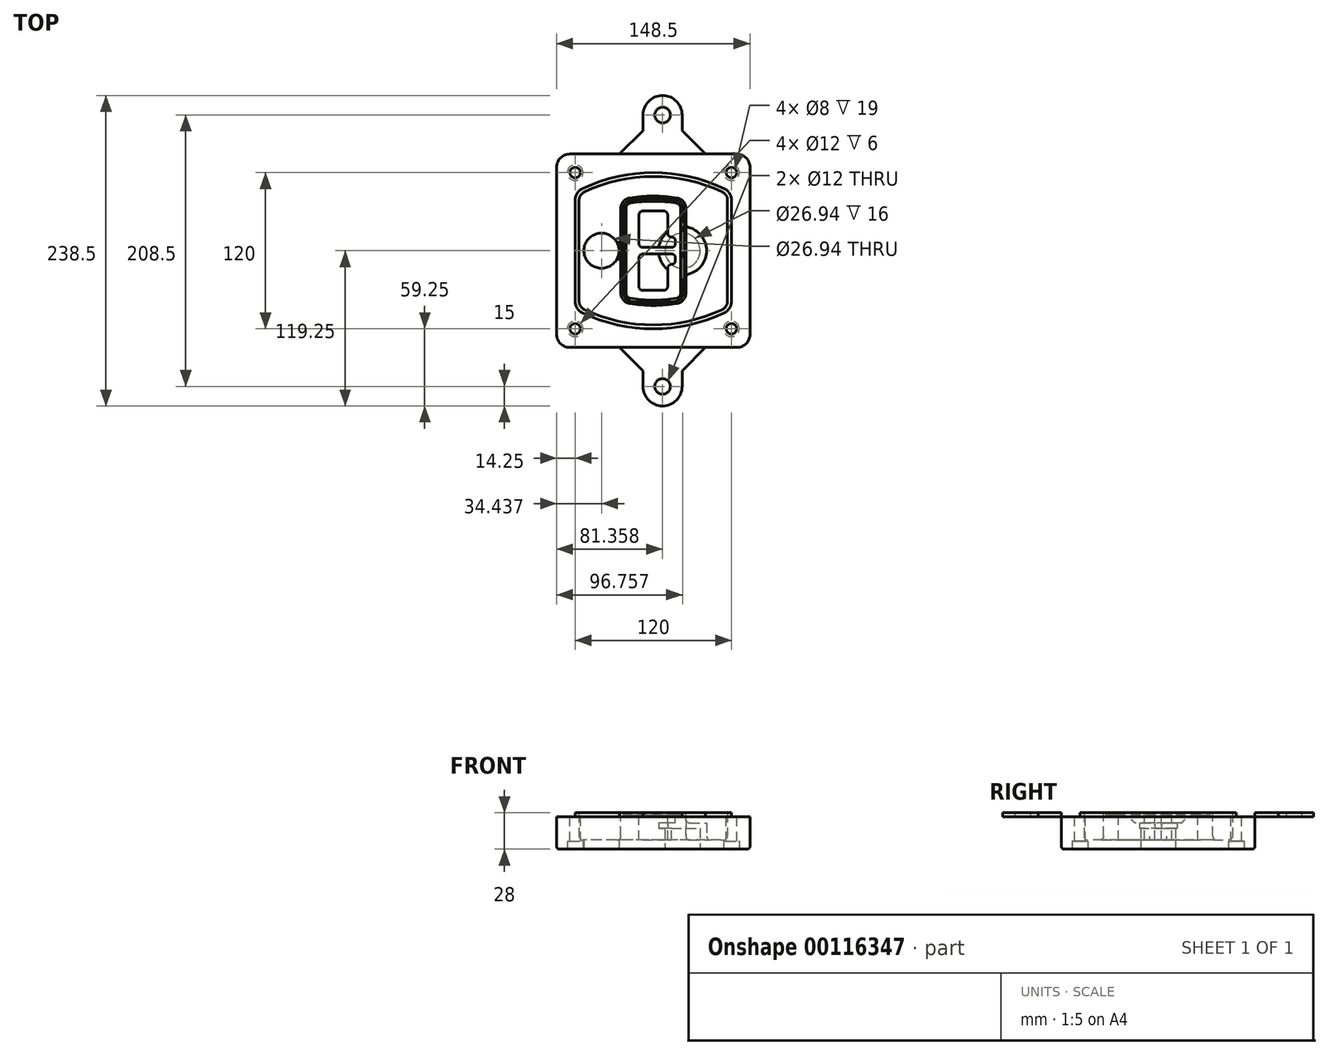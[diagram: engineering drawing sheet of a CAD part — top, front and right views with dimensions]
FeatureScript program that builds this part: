
annotation { "Feature Type Name" : "Feature", "Feature Type Description" : "" }
export const myFeature = defineFeature(function(context is Context, id is Id, definition is map)
    precondition{}
    {
        {
            var Q0;
            Q0=qCreatedBy(makeId("Top.planeOp"),FACE);
            var sketch = newSketch(context, id + "F0", { "sketchPlane" : qUnion([Q0])});
            skPoint(sketch, "E0.rect.middle", {"position": v(0, 0) * mm});
            skLineSegment(sketch, "E1.bottom", {"start": v(-64.25, -74.25) * mm, "end": v(64.25, -74.25) * mm});
            skLineSegment(sketch, "E1.top", {"start": v(-64.25, 74.25) * mm, "end": v(64.25, 74.25) * mm});
            skLineSegment(sketch, "E1.left", {"start": v(-74.25, -64.25) * mm, "end": v(-74.25, 64.25) * mm});
            skLineSegment(sketch, "E1.right", {"start": v(74.25, -64.25) * mm, "end": v(74.25, 64.25) * mm});
            skLineSegment(sketch, "E2", {"start": v(-74.25, 74.25) * mm, "end": v(74.25, -74.25) * mm, "construction": true});
            skLineSegment(sketch, "E3", {"start": v(74.25, 74.25) * mm, "end": v(-74.25, -74.25) * mm, "construction": true});
            skCircle(sketch, "E4", {"center": v(-60, 60) * mm, "radius": 4 * mm});
            skCircle(sketch, "E5", {"center": v(60, 60) * mm, "radius": 4 * mm});
            skCircle(sketch, "E6", {"center": v(60, -60) * mm, "radius": 4 * mm});
            skCircle(sketch, "E7", {"center": v(-60, -60) * mm, "radius": 4 * mm});
            skLineSegment(sketch, "E8", {"start": v(-60, 60) * mm, "end": v(60, 60) * mm, "construction": true});
            skLineSegment(sketch, "E9", {"start": v(60, 60) * mm, "end": v(60, -60) * mm, "construction": true});
            skLineSegment(sketch, "E10", {"start": v(60, -60) * mm, "end": v(-60, -60) * mm, "construction": true});
            skLineSegment(sketch, "E11", {"start": v(-60, -60) * mm, "end": v(-60, 60) * mm, "construction": true});
            skLineSegment(sketch, "E12", {"start": v(-60, 38.83) * mm, "end": v(-60, -38.83) * mm});
            skLineSegment(sketch, "E13", {"start": v(60, 38.83) * mm, "end": v(60, -38.83) * mm});
            skArc(sketch, "E14", {"start": v(54.26, 47.88) * mm, "mid": v(0, 60) * mm, "end": v(-54.26, 47.88) * mm});
            skArc(sketch, "E15", {"start": v(-54.26, -47.88) * mm, "mid": v(0, -60) * mm, "end": v(54.26, -47.88) * mm});
            skLineSegment(sketch, "E16", {"start": v(-60, 0) * mm, "end": v(60, 0) * mm, "construction": true});
            skPoint(sketch, "E17.visualSharp", {"position": v(-60, -45) * mm});
            skArc(sketch, "E17.filletArc", {"start": v(-60, -38.83) * mm, "mid": v(-58.44, -44.2) * mm, "end": v(-54.26, -47.88) * mm});
            skPoint(sketch, "E18.visualSharp", {"position": v(-60, 45) * mm});
            skArc(sketch, "E18.filletArc", {"start": v(-54.26, 47.88) * mm, "mid": v(-58.44, 44.2) * mm, "end": v(-60, 38.83) * mm});
            skPoint(sketch, "E19.visualSharp", {"position": v(60, 45) * mm});
            skArc(sketch, "E19.filletArc", {"start": v(60, 38.83) * mm, "mid": v(58.44, 44.2) * mm, "end": v(54.26, 47.88) * mm});
            skPoint(sketch, "E20.visualSharp", {"position": v(60, -45) * mm});
            skArc(sketch, "E20.filletArc", {"start": v(54.26, -47.88) * mm, "mid": v(58.44, -44.2) * mm, "end": v(60, -38.83) * mm});
            skPoint(sketch, "E21.visualSharp", {"position": v(-74.25, 74.25) * mm});
            skArc(sketch, "E21.filletArc", {"start": v(-64.25, 74.25) * mm, "mid": v(-71.32, 71.32) * mm, "end": v(-74.25, 64.25) * mm});
            skPoint(sketch, "E22.visualSharp", {"position": v(74.25, 74.25) * mm});
            skArc(sketch, "E22.filletArc", {"start": v(74.25, 64.25) * mm, "mid": v(71.32, 71.32) * mm, "end": v(64.25, 74.25) * mm});
            skPoint(sketch, "E23.visualSharp", {"position": v(74.25, -74.25) * mm});
            skArc(sketch, "E23.filletArc", {"start": v(64.25, -74.25) * mm, "mid": v(71.32, -71.32) * mm, "end": v(74.25, -64.25) * mm});
            skPoint(sketch, "E24.visualSharp", {"position": v(-74.25, -74.25) * mm});
            skArc(sketch, "E24.filletArc", {"start": v(-74.25, -64.25) * mm, "mid": v(-71.32, -71.32) * mm, "end": v(-64.25, -74.25) * mm});
            skArc(sketch, "E25.0", {"start": v(57, 38.83) * mm, "mid": v(55.9, 42.58) * mm, "end": v(52.98, 45.17) * mm});
            skLineSegment(sketch, "E25.1", {"start": v(57, 38.83) * mm, "end": v(57, -38.83) * mm});
            skArc(sketch, "E25.2", {"start": v(52.98, -45.17) * mm, "mid": v(55.9, -42.58) * mm, "end": v(57, -38.83) * mm});
            skArc(sketch, "E25.3", {"start": v(-52.98, -45.17) * mm, "mid": v(0, -57) * mm, "end": v(52.98, -45.17) * mm});
            skArc(sketch, "E25.4", {"start": v(-57, -38.83) * mm, "mid": v(-55.9, -42.58) * mm, "end": v(-52.98, -45.17) * mm});
            skArc(sketch, "E25.5", {"start": v(52.98, 45.17) * mm, "mid": v(0, 57) * mm, "end": v(-52.98, 45.17) * mm});
            skLineSegment(sketch, "E25.6", {"start": v(-57, 38.83) * mm, "end": v(-57, -38.83) * mm});
            skArc(sketch, "E25.7", {"start": v(-52.98, 45.17) * mm, "mid": v(-55.9, 42.58) * mm, "end": v(-57, 38.83) * mm});
            skArc(sketch, "E26.0", {"start": v(-55.96, 51.5) * mm, "mid": v(-61.82, 46.33) * mm, "end": v(-64, 38.83) * mm});
            skArc(sketch, "E26.1", {"start": v(55.96, 51.5) * mm, "mid": v(0, 64) * mm, "end": v(-55.96, 51.5) * mm});
            skArc(sketch, "E26.2", {"start": v(64, 38.83) * mm, "mid": v(61.82, 46.33) * mm, "end": v(55.96, 51.5) * mm});
            skLineSegment(sketch, "E26.3", {"start": v(64, 38.83) * mm, "end": v(64, -38.83) * mm});
            skArc(sketch, "E26.4", {"start": v(55.96, -51.5) * mm, "mid": v(61.82, -46.33) * mm, "end": v(64, -38.83) * mm});
            skLineSegment(sketch, "E26.5", {"start": v(-64, 38.83) * mm, "end": v(-64, -38.83) * mm});
            skArc(sketch, "E26.6", {"start": v(-55.96, -51.5) * mm, "mid": v(0, -64) * mm, "end": v(55.96, -51.5) * mm});
            skArc(sketch, "E26.7", {"start": v(-64, -38.83) * mm, "mid": v(-61.82, -46.33) * mm, "end": v(-55.96, -51.5) * mm});
            skSolve(sketch);
        }
        {
            var Q0;
            Q0=makeQuery(id+"F0.imprint","IMPRINT",FACE,{"disambiguationData":[TD([[makeQuery(id+"F0.imprint","IMPRINT",EDGE,{"derivedFrom":sQuery(id+"F0.wireOp",EDGE,"E1.bottom")}),1.0]])]});
            var Q1;
            Q1=makeQuery(id+"F0.imprint","IMPRINT",FACE,{"disambiguationData":[TD([[makeQuery(id+"F0.imprint","IMPRINT",EDGE,{"derivedFrom":sQuery(id+"F0.wireOp",EDGE,"E12")}),1.0]])]});
            var Q2;
            Q2=makeQuery(id+"F0.imprint","IMPRINT",FACE,{"disambiguationData":[TD([[makeQuery(id+"F0.imprint","IMPRINT",EDGE,{"derivedFrom":sQuery(id+"F0.wireOp",EDGE,"E25.0")}),1.0]])]});
            var Q3;
            Q3=makeQuery(id+"F0.imprint","IMPRINT",FACE,{"disambiguationData":[TD([[makeQuery(id+"F0.imprint","IMPRINT",EDGE,{"derivedFrom":sQuery(id+"F0.wireOp",EDGE,"E12")}),-1.0]])]});
            extrude(context, id + "F1", {"entities" : qUnion([Q0, Q1, Q2, Q3]), "oppositeDirection" : true, "depth" : 25 * mm});
        }
        {
            var Q0;
            Q0=makeQuery(id+"F0.imprint","IMPRINT",FACE,{"disambiguationData":[TD([[makeQuery(id+"F0.imprint","IMPRINT",EDGE,{"derivedFrom":sQuery(id+"F0.wireOp",EDGE,"E12")}),1.0]])]});
            extrude(context, id + "F2", {"entities" : qUnion([Q0]), "operationType" : NewBodyOperationType.ADD, "depth" : 3 * mm});
        }
        {
            var Q0;
            Q0=makeQuery(id+"F0.imprint","IMPRINT",FACE,{"disambiguationData":[TD([[makeQuery(id+"F0.imprint","IMPRINT",EDGE,{"derivedFrom":sQuery(id+"F0.wireOp",EDGE,"E25.0")}),1.0]])]});
            extrude(context, id + "F3", {"entities" : qUnion([Q0]), "operationType" : NewBodyOperationType.REMOVE, "oppositeDirection" : true, "depth" : 18 * mm});
        }
        {
            var Q0;
            Q0=makeQuery(id+"F2.opExtrude","CAP_FACE",FACE,{"disambiguationData":[OSD([sQuery(id+"F0.wireOp",EDGE,"E12"),sQuery(id+"F0.wireOp",EDGE,"E13"),sQuery(id+"F0.wireOp",EDGE,"E14"),sQuery(id+"F0.wireOp",EDGE,"E15"),sQuery(id+"F0.wireOp",EDGE,"E17.filletArc"),sQuery(id+"F0.wireOp",EDGE,"E18.filletArc"),sQuery(id+"F0.wireOp",EDGE,"E19.filletArc"),sQuery(id+"F0.wireOp",EDGE,"E20.filletArc"),sQuery(id+"F0.wireOp",EDGE,"E25.0"),sQuery(id+"F0.wireOp",EDGE,"E25.1"),sQuery(id+"F0.wireOp",EDGE,"E25.2"),sQuery(id+"F0.wireOp",EDGE,"E25.3"),sQuery(id+"F0.wireOp",EDGE,"E25.4"),sQuery(id+"F0.wireOp",EDGE,"E25.5"),sQuery(id+"F0.wireOp",EDGE,"E25.6"),sQuery(id+"F0.wireOp",EDGE,"E25.7")])],"isStart":false});
            var sketch = newSketch(context, id + "F4", { "sketchPlane" : qUnion([Q0])});
            skArc(sketch, "E27.0", {"start": v(-18.34, -40.45) * mm, "mid": v(0, -42) * mm, "end": v(18.34, -40.45) * mm});
            skArc(sketch, "E28.0", {"start": v(18.34, 40.45) * mm, "mid": v(0, 42) * mm, "end": v(-18.34, 40.45) * mm});
            skLineSegment(sketch, "E29", {"start": v(-25, 32.57) * mm, "end": v(-25, -32.57) * mm});
            skLineSegment(sketch, "E30", {"start": v(25, 32.57) * mm, "end": v(25, -32.57) * mm});
            skLineSegment(sketch, "E31", {"start": v(-25, 39.1) * mm, "end": v(25, 39.1) * mm, "construction": true});
            skLineSegment(sketch, "E32", {"start": v(-25, -39.1) * mm, "end": v(25, -39.1) * mm, "construction": true});
            skPoint(sketch, "E33.visualSharp", {"position": v(-25, 39.1) * mm});
            skArc(sketch, "E33.filletArc", {"start": v(-18.34, 40.45) * mm, "mid": v(-23.11, 37.73) * mm, "end": v(-25, 32.57) * mm});
            skPoint(sketch, "E34.visualSharp", {"position": v(25, 39.1) * mm});
            skArc(sketch, "E34.filletArc", {"start": v(25, 32.57) * mm, "mid": v(23.11, 37.73) * mm, "end": v(18.34, 40.45) * mm});
            skPoint(sketch, "E35.visualSharp", {"position": v(25, -39.1) * mm});
            skArc(sketch, "E35.filletArc", {"start": v(18.34, -40.45) * mm, "mid": v(23.11, -37.73) * mm, "end": v(25, -32.57) * mm});
            skPoint(sketch, "E36.visualSharp", {"position": v(-25, -39.1) * mm});
            skArc(sketch, "E36.filletArc", {"start": v(-25, -32.57) * mm, "mid": v(-23.11, -37.73) * mm, "end": v(-18.34, -40.45) * mm});
            skArc(sketch, "E37.0", {"start": v(52.98, 45.17) * mm, "mid": v(0, 57) * mm, "end": v(-52.98, 45.17) * mm});
            skArc(sketch, "E37.1", {"start": v(-52.98, 45.17) * mm, "mid": v(-55.9, 42.58) * mm, "end": v(-57, 38.83) * mm});
            skLineSegment(sketch, "E37.2", {"start": v(-57, 38.83) * mm, "end": v(-57, -38.83) * mm});
            skArc(sketch, "E37.3", {"start": v(-57, -38.83) * mm, "mid": v(-55.9, -42.58) * mm, "end": v(-52.98, -45.17) * mm});
            skArc(sketch, "E37.4", {"start": v(-52.98, -45.17) * mm, "mid": v(0, -57) * mm, "end": v(52.98, -45.17) * mm});
            skArc(sketch, "E37.5", {"start": v(52.98, -45.17) * mm, "mid": v(55.9, -42.58) * mm, "end": v(57, -38.83) * mm});
            skLineSegment(sketch, "E37.6", {"start": v(57, 38.83) * mm, "end": v(57, -38.83) * mm});
            skArc(sketch, "E37.7", {"start": v(57, 38.83) * mm, "mid": v(55.9, 42.58) * mm, "end": v(52.98, 45.17) * mm});
            skLineSegment(sketch, "E38.0", {"start": v(23, 32.57) * mm, "end": v(23, -32.57) * mm});
            skArc(sketch, "E38.1", {"start": v(18, -38.48) * mm, "mid": v(21.58, -36.44) * mm, "end": v(23, -32.57) * mm});
            skArc(sketch, "E38.2", {"start": v(-18, -38.48) * mm, "mid": v(0, -40) * mm, "end": v(18, -38.48) * mm});
            skArc(sketch, "E38.3", {"start": v(-23, -32.57) * mm, "mid": v(-21.58, -36.44) * mm, "end": v(-18, -38.48) * mm});
            skLineSegment(sketch, "E38.4", {"start": v(-23, 32.57) * mm, "end": v(-23, -32.57) * mm});
            skArc(sketch, "E38.5", {"start": v(23, 32.57) * mm, "mid": v(21.58, 36.44) * mm, "end": v(18, 38.48) * mm});
            skArc(sketch, "E38.6", {"start": v(-18, 38.48) * mm, "mid": v(-21.58, 36.44) * mm, "end": v(-23, 32.57) * mm});
            skArc(sketch, "E38.7", {"start": v(18, 38.48) * mm, "mid": v(0, 40) * mm, "end": v(-18, 38.48) * mm});
            skArc(sketch, "E39.0", {"start": v(21, 32.57) * mm, "mid": v(20.06, 35.15) * mm, "end": v(17.67, 36.5) * mm});
            skLineSegment(sketch, "E39.1", {"start": v(21, 32.57) * mm, "end": v(21, -32.57) * mm});
            skArc(sketch, "E39.2", {"start": v(17.67, -36.5) * mm, "mid": v(20.06, -35.15) * mm, "end": v(21, -32.57) * mm});
            skArc(sketch, "E39.3", {"start": v(-17.67, -36.5) * mm, "mid": v(0, -38) * mm, "end": v(17.67, -36.5) * mm});
            skArc(sketch, "E39.4", {"start": v(-21, -32.57) * mm, "mid": v(-20.06, -35.15) * mm, "end": v(-17.67, -36.5) * mm});
            skArc(sketch, "E39.5", {"start": v(17.67, 36.5) * mm, "mid": v(0, 38) * mm, "end": v(-17.67, 36.5) * mm});
            skLineSegment(sketch, "E39.6", {"start": v(-21, 32.57) * mm, "end": v(-21, -32.57) * mm});
            skArc(sketch, "E39.7", {"start": v(-17.67, 36.5) * mm, "mid": v(-20.06, 35.15) * mm, "end": v(-21, 32.57) * mm});
            skLineSegment(sketch, "E40", {"start": v(-25, 0) * mm, "end": v(25, 0) * mm, "construction": true});
            skLineSegment(sketch, "E41", {"start": v(-11, 5.5) * mm, "end": v(-11, 27.5) * mm});
            skLineSegment(sketch, "E42", {"start": v(-8, 30.5) * mm, "end": v(8, 30.5) * mm});
            skLineSegment(sketch, "E43", {"start": v(11, 27.5) * mm, "end": v(11, 13.5) * mm});
            skLineSegment(sketch, "E44", {"start": v(14, 10.5) * mm, "end": v(14, 10.5) * mm});
            skLineSegment(sketch, "E45", {"start": v(17, 7.5) * mm, "end": v(17, 5.5) * mm});
            skLineSegment(sketch, "E46", {"start": v(14, 2.5) * mm, "end": v(-8, 2.5) * mm});
            skPoint(sketch, "E47.visualSharp", {"position": v(-11, 30.5) * mm});
            skArc(sketch, "E47.filletArc", {"start": v(-8, 30.5) * mm, "mid": v(-10.12, 29.62) * mm, "end": v(-11, 27.5) * mm});
            skPoint(sketch, "E48.visualSharp", {"position": v(11, 30.5) * mm});
            skArc(sketch, "E48.filletArc", {"start": v(11, 27.5) * mm, "mid": v(10.12, 29.62) * mm, "end": v(8, 30.5) * mm});
            skPoint(sketch, "E49.visualSharp", {"position": v(11, 10.5) * mm});
            skArc(sketch, "E49.filletArc", {"start": v(11, 13.5) * mm, "mid": v(11.88, 11.38) * mm, "end": v(14, 10.5) * mm});
            skPoint(sketch, "E50.visualSharp", {"position": v(17, 10.5) * mm});
            skArc(sketch, "E50.filletArc", {"start": v(17, 7.5) * mm, "mid": v(16.12, 9.62) * mm, "end": v(14, 10.5) * mm});
            skPoint(sketch, "E51.visualSharp", {"position": v(17, 2.5) * mm});
            skArc(sketch, "E51.filletArc", {"start": v(14, 2.5) * mm, "mid": v(16.12, 3.38) * mm, "end": v(17, 5.5) * mm});
            skPoint(sketch, "E52.visualSharp", {"position": v(-11, 2.5) * mm});
            skArc(sketch, "E52.filletArc", {"start": v(-11, 5.5) * mm, "mid": v(-10.12, 3.38) * mm, "end": v(-8, 2.5) * mm});
            skLineSegment(sketch, "E53.0.MirrorCS", {"start": v(14, -2.5) * mm, "end": v(-8, -2.5) * mm});
            skArc(sketch, "E54.0.MirrorCS", {"start": v(-11, -5.5) * mm, "mid": v(-10.12, -3.38) * mm, "end": v(-8, -2.5) * mm});
            skLineSegment(sketch, "E55.0.MirrorCS", {"start": v(-11, -5.5) * mm, "end": v(-11, -27.5) * mm});
            skArc(sketch, "E56.0.MirrorCS", {"start": v(-8, -30.5) * mm, "mid": v(-10.12, -29.62) * mm, "end": v(-11, -27.5) * mm});
            skLineSegment(sketch, "E57.0.MirrorCS", {"start": v(-8, -30.5) * mm, "end": v(8, -30.5) * mm});
            skArc(sketch, "E58.0.MirrorCS", {"start": v(11, -27.5) * mm, "mid": v(10.12, -29.62) * mm, "end": v(8, -30.5) * mm});
            skLineSegment(sketch, "E59.0.MirrorCS", {"start": v(11, -27.5) * mm, "end": v(11, -13.5) * mm});
            skArc(sketch, "E60.0.MirrorCS", {"start": v(11, -13.5) * mm, "mid": v(11.88, -11.38) * mm, "end": v(14, -10.5) * mm});
            skArc(sketch, "E61.0.MirrorCS", {"start": v(17, -7.5) * mm, "mid": v(16.12, -9.62) * mm, "end": v(14, -10.5) * mm});
            skLineSegment(sketch, "E62.0.MirrorCS", {"start": v(17, -7.5) * mm, "end": v(17, -5.5) * mm});
            skArc(sketch, "E63.0.MirrorCS", {"start": v(14, -2.5) * mm, "mid": v(16.12, -3.38) * mm, "end": v(17, -5.5) * mm});
            skSolve(sketch);
        }
        {
            var Q0;
            Q0=makeQuery(id+"F4.imprint","IMPRINT",FACE,{"disambiguationData":[TD([[makeQuery(id+"F4.imprint","IMPRINT",EDGE,{"derivedFrom":sQuery(id+"F4.wireOp",EDGE,"E27.0")}),1.0]])]});
            var Q1;
            Q1=makeQuery(id+"F4.imprint","IMPRINT",FACE,{"disambiguationData":[TD([[makeQuery(id+"F4.imprint","IMPRINT",EDGE,{"derivedFrom":sQuery(id+"F4.wireOp",EDGE,"E38.0")}),-1.0]])]});
            var Q2;
            Q2=makeQuery(id+"F4.imprint","IMPRINT",FACE,{"disambiguationData":[TD([[makeQuery(id+"F4.imprint","IMPRINT",EDGE,{"derivedFrom":sQuery(id+"F4.wireOp",EDGE,"E39.0")}),1.0]])]});
            extrude(context, id + "F5", {"entities" : qUnion([Q0, Q1, Q2]), "operationType" : NewBodyOperationType.ADD, "endBound" : BoundingType.UP_TO_NEXT, "oppositeDirection" : true, "depth" : 25 * mm});
        }
        {
            var Q0;
            Q0=makeQuery(id+"F4.imprint","IMPRINT",FACE,{"disambiguationData":[TD([[makeQuery(id+"F4.imprint","IMPRINT",EDGE,{"derivedFrom":sQuery(id+"F4.wireOp",EDGE,"E38.0")}),-1.0]])]});
            extrude(context, id + "F6", {"entities" : qUnion([Q0]), "operationType" : NewBodyOperationType.REMOVE, "oppositeDirection" : true, "depth" : 2 * mm});
        }
        {
            var Q0;
            Q0=makeQuery(id+"F1.opExtrude","CAP_FACE",FACE,{"disambiguationData":[OSD([sQuery(id+"F0.wireOp",EDGE,"E1.bottom"),sQuery(id+"F0.wireOp",EDGE,"E1.top"),sQuery(id+"F0.wireOp",EDGE,"E1.left"),sQuery(id+"F0.wireOp",EDGE,"E1.right"),sQuery(id+"F0.wireOp",EDGE,"E4"),sQuery(id+"F0.wireOp",EDGE,"E5"),sQuery(id+"F0.wireOp",EDGE,"E6"),sQuery(id+"F0.wireOp",EDGE,"E7"),sQuery(id+"F0.wireOp",EDGE,"E21.filletArc"),sQuery(id+"F0.wireOp",EDGE,"E22.filletArc"),sQuery(id+"F0.wireOp",EDGE,"E23.filletArc"),sQuery(id+"F0.wireOp",EDGE,"E24.filletArc")])],"isStart":false});
            var sketch = newSketch(context, id + "F7", { "sketchPlane" : qUnion([Q0])});
            skCircle(sketch, "E64", {"center": v(22.5, 0) * mm, "radius": 13.47 * mm});
            skCircle(sketch, "E65", {"center": v(-39.81, 0) * mm, "radius": 13.47 * mm});
            skLineSegment(sketch, "E66", {"start": v(74.25, 0) * mm, "end": v(-74.25, 0) * mm});
            skCircle(sketch, "E67", {"center": v(22.5, 0) * mm, "radius": 18.47 * mm});
            skCircle(sketch, "E68", {"center": v(60, -60) * mm, "radius": 6 * mm});
            skCircle(sketch, "E69", {"center": v(-60, -60) * mm, "radius": 6 * mm});
            skCircle(sketch, "E70", {"center": v(-60, 60) * mm, "radius": 6 * mm});
            skCircle(sketch, "E71", {"center": v(60, 60) * mm, "radius": 6 * mm});
            skSolve(sketch);
        }
        {
            var Q0;
            {var subQ1=sQuery(id+"F7.wireOp",EDGE,"E66");var subQ4=sQuery(id+"F7.wireOp",EDGE,"E64");var subQ6=makeQuery(id+"F7.imprint","INTERSECT",VERTEX,{"disambiguationData":[OD(0.0)],"derivedFrom":[subQ4,subQ1]});Q0=makeQuery(id+"F7.imprint","IMPRINT",FACE,{"disambiguationData":[TD([[makeQuery(id+"F7.imprint","IMPRINT",EDGE,{"disambiguationData":[TD([[subQ6,-1.0]])],"derivedFrom":subQ4}),-1.0]])]});}
            var Q1;
            {var subQ0=sQuery(id+"F7.wireOp",EDGE,"E66");var subQ1=sQuery(id+"F7.wireOp",EDGE,"E64");var subQ3=makeQuery(id+"F7.imprint","INTERSECT",VERTEX,{"disambiguationData":[OD(0.0)],"derivedFrom":[subQ1,subQ0]});Q1=makeQuery(id+"F7.imprint","IMPRINT",FACE,{"disambiguationData":[TD([[makeQuery(id+"F7.imprint","IMPRINT",EDGE,{"disambiguationData":[TD([[subQ3,-1.0]])],"derivedFrom":subQ1}),1.0]])]});}
            var Q2;
            {var subQ0=sQuery(id+"F7.wireOp",EDGE,"E66");var subQ1=sQuery(id+"F7.wireOp",EDGE,"E64");var subQ3=makeQuery(id+"F7.imprint","INTERSECT",VERTEX,{"disambiguationData":[OD(0.0)],"derivedFrom":[subQ1,subQ0]});Q2=makeQuery(id+"F7.imprint","IMPRINT",FACE,{"disambiguationData":[TD([[makeQuery(id+"F7.imprint","IMPRINT",EDGE,{"disambiguationData":[TD([[subQ3,1.0]])],"derivedFrom":subQ1}),1.0]])]});}
            var Q3;
            {var subQ1=sQuery(id+"F7.wireOp",EDGE,"E66");var subQ4=sQuery(id+"F7.wireOp",EDGE,"E64");var subQ6=makeQuery(id+"F7.imprint","INTERSECT",VERTEX,{"disambiguationData":[OD(0.0)],"derivedFrom":[subQ4,subQ1]});Q3=makeQuery(id+"F7.imprint","IMPRINT",FACE,{"disambiguationData":[TD([[makeQuery(id+"F7.imprint","IMPRINT",EDGE,{"disambiguationData":[TD([[subQ6,1.0]])],"derivedFrom":subQ4}),-1.0]])]});}
            extrude(context, id + "F8", {"entities" : qUnion([Q0, Q1, Q2, Q3]), "operationType" : NewBodyOperationType.ADD, "oppositeDirection" : true, "depth" : 20 * mm});
        }
        {
            var Q0;
            {var subQ0=sQuery(id+"F7.wireOp",EDGE,"E66");var subQ1=sQuery(id+"F7.wireOp",EDGE,"E64");var subQ3=makeQuery(id+"F7.imprint","INTERSECT",VERTEX,{"disambiguationData":[OD(0.0)],"derivedFrom":[subQ1,subQ0]});Q0=makeQuery(id+"F7.imprint","IMPRINT",FACE,{"disambiguationData":[TD([[makeQuery(id+"F7.imprint","IMPRINT",EDGE,{"disambiguationData":[TD([[subQ3,-1.0]])],"derivedFrom":subQ1}),1.0]])]});}
            var Q1;
            {var subQ0=sQuery(id+"F7.wireOp",EDGE,"E66");var subQ1=sQuery(id+"F7.wireOp",EDGE,"E64");var subQ3=makeQuery(id+"F7.imprint","INTERSECT",VERTEX,{"disambiguationData":[OD(0.0)],"derivedFrom":[subQ1,subQ0]});Q1=makeQuery(id+"F7.imprint","IMPRINT",FACE,{"disambiguationData":[TD([[makeQuery(id+"F7.imprint","IMPRINT",EDGE,{"disambiguationData":[TD([[subQ3,1.0]])],"derivedFrom":subQ1}),1.0]])]});}
            extrude(context, id + "F9", {"entities" : qUnion([Q0, Q1]), "operationType" : NewBodyOperationType.REMOVE, "oppositeDirection" : true, "depth" : 16 * mm});
        }
        {
            var Q0;
            {var subQ0=sQuery(id+"F7.wireOp",EDGE,"E66");var subQ1=sQuery(id+"F7.wireOp",EDGE,"E65");var subQ3=makeQuery(id+"F7.imprint","INTERSECT",VERTEX,{"disambiguationData":[OD(0.0)],"derivedFrom":[subQ1,subQ0]});Q0=makeQuery(id+"F7.imprint","IMPRINT",FACE,{"disambiguationData":[TD([[makeQuery(id+"F7.imprint","IMPRINT",EDGE,{"disambiguationData":[TD([[subQ3,-1.0]])],"derivedFrom":subQ1}),1.0]])]});}
            var Q1;
            {var subQ0=sQuery(id+"F7.wireOp",EDGE,"E66");var subQ1=sQuery(id+"F7.wireOp",EDGE,"E65");var subQ3=makeQuery(id+"F7.imprint","INTERSECT",VERTEX,{"disambiguationData":[OD(0.0)],"derivedFrom":[subQ1,subQ0]});Q1=makeQuery(id+"F7.imprint","IMPRINT",FACE,{"disambiguationData":[TD([[makeQuery(id+"F7.imprint","IMPRINT",EDGE,{"disambiguationData":[TD([[subQ3,1.0]])],"derivedFrom":subQ1}),1.0]])]});}
            extrude(context, id + "F10", {"entities" : qUnion([Q0, Q1]), "operationType" : NewBodyOperationType.REMOVE, "oppositeDirection" : true, "depth" : 25 * mm});
        }
        {
            var Q0;
            Q0=makeQuery(id+"F7.imprint","IMPRINT",FACE,{"disambiguationData":[TD([[makeQuery(id+"F7.imprint","IMPRINT",EDGE,{"derivedFrom":sQuery(id+"F7.wireOp",EDGE,"E68")}),1.0]])]});
            var Q1;
            Q1=makeQuery(id+"F7.imprint","IMPRINT",FACE,{"disambiguationData":[TD([[makeQuery(id+"F7.imprint","IMPRINT",EDGE,{"derivedFrom":makeQuery(id+"F1.opExtrude","CAP_EDGE",EDGE,{"disambiguationData":[OSD([sQuery(id+"F0.wireOp",EDGE,"E5")])],"isStart":false})}),-1.0]])]});
            var Q2;
            Q2=makeQuery(id+"F7.imprint","IMPRINT",FACE,{"disambiguationData":[TD([[makeQuery(id+"F7.imprint","IMPRINT",EDGE,{"derivedFrom":sQuery(id+"F7.wireOp",EDGE,"E69")}),1.0]])]});
            var Q3;
            Q3=makeQuery(id+"F7.imprint","IMPRINT",FACE,{"disambiguationData":[TD([[makeQuery(id+"F7.imprint","IMPRINT",EDGE,{"derivedFrom":makeQuery(id+"F1.opExtrude","CAP_EDGE",EDGE,{"disambiguationData":[OSD([sQuery(id+"F0.wireOp",EDGE,"E4")])],"isStart":false})}),-1.0]])]});
            var Q4;
            Q4=makeQuery(id+"F7.imprint","IMPRINT",FACE,{"disambiguationData":[TD([[makeQuery(id+"F7.imprint","IMPRINT",EDGE,{"derivedFrom":sQuery(id+"F7.wireOp",EDGE,"E70")}),1.0]])]});
            var Q5;
            Q5=makeQuery(id+"F7.imprint","IMPRINT",FACE,{"disambiguationData":[TD([[makeQuery(id+"F7.imprint","IMPRINT",EDGE,{"derivedFrom":makeQuery(id+"F1.opExtrude","CAP_EDGE",EDGE,{"disambiguationData":[OSD([sQuery(id+"F0.wireOp",EDGE,"E7")])],"isStart":false})}),-1.0]])]});
            var Q6;
            Q6=makeQuery(id+"F7.imprint","IMPRINT",FACE,{"disambiguationData":[TD([[makeQuery(id+"F7.imprint","IMPRINT",EDGE,{"derivedFrom":sQuery(id+"F7.wireOp",EDGE,"E71")}),1.0]])]});
            var Q7;
            Q7=makeQuery(id+"F7.imprint","IMPRINT",FACE,{"disambiguationData":[TD([[makeQuery(id+"F7.imprint","IMPRINT",EDGE,{"derivedFrom":makeQuery(id+"F1.opExtrude","CAP_EDGE",EDGE,{"disambiguationData":[OSD([sQuery(id+"F0.wireOp",EDGE,"E6")])],"isStart":false})}),-1.0]])]});
            extrude(context, id + "F11", {"entities" : qUnion([Q0, Q1, Q2, Q3, Q4, Q5, Q6, Q7]), "operationType" : NewBodyOperationType.REMOVE, "oppositeDirection" : true, "depth" : 6 * mm});
        }
        {
            var Q0;
            Q0=makeQuery(id+"F9.boolean.opBoolean","COPY",FACE,{"derivedFrom":makeQuery(id+"F9.opExtrude","CAP_FACE",FACE,{"disambiguationData":[OSD([sQuery(id+"F7.wireOp",EDGE,"E64")])],"isStart":false})});
            var sketch = newSketch(context, id + "F12", { "sketchPlane" : qUnion([Q0])});
            skArc(sketch, "E72.0", {"start": v(11, 14.45) * mm, "mid": v(6.45, 9.13) * mm, "end": v(4.2, 2.5) * mm});
            skArc(sketch, "E72.1", {"start": v(4.2, -2.5) * mm, "mid": v(6.45, -9.13) * mm, "end": v(11, -14.45) * mm});
            skLineSegment(sketch, "E73", {"start": v(4.2, -2.5) * mm, "end": v(14, -2.5) * mm});
            skLineSegment(sketch, "E74.0", {"start": v(14, 2.5) * mm, "end": v(4.2, 2.5) * mm});
            skArc(sketch, "E74.1", {"start": v(14, 2.5) * mm, "mid": v(16.12, 3.38) * mm, "end": v(17, 5.5) * mm});
            skLineSegment(sketch, "E74.2", {"start": v(17, 7.5) * mm, "end": v(17, 5.5) * mm});
            skArc(sketch, "E74.3", {"start": v(17, 7.5) * mm, "mid": v(16.12, 9.62) * mm, "end": v(14, 10.5) * mm});
            skArc(sketch, "E74.4", {"start": v(11, 13.5) * mm, "mid": v(11.88, 11.38) * mm, "end": v(14, 10.5) * mm});
            skLineSegment(sketch, "E74.5", {"start": v(11, 14.45) * mm, "end": v(11, 13.5) * mm});
            skLineSegment(sketch, "E74.7", {"start": v(14, -2.5) * mm, "end": v(4.2, -2.5) * mm});
            skArc(sketch, "E74.8", {"start": v(14, -2.5) * mm, "mid": v(16.12, -3.38) * mm, "end": v(17, -5.5) * mm});
            skLineSegment(sketch, "E74.9", {"start": v(17, -7.5) * mm, "end": v(17, -5.5) * mm});
            skArc(sketch, "E74.10", {"start": v(17, -7.5) * mm, "mid": v(16.12, -9.62) * mm, "end": v(14, -10.5) * mm});
            skArc(sketch, "E74.11", {"start": v(11, -13.5) * mm, "mid": v(11.88, -11.38) * mm, "end": v(14, -10.5) * mm});
            skLineSegment(sketch, "E74.12", {"start": v(11, -14.45) * mm, "end": v(11, -13.5) * mm});
            skPoint(sketch, "E75.orphan", {"position": v(11, -27.5) * mm});
            skPoint(sketch, "E76.orphan", {"position": v(-8, -2.5) * mm});
            skPoint(sketch, "E77.orphan", {"position": v(-8, 2.5) * mm});
            skPoint(sketch, "E78.orphan", {"position": v(11, 27.5) * mm});
            skSolve(sketch);
        }
        {
            var Q0;
            {var subQ7=sQuery(id+"F12.wireOp",EDGE,"E72.0");var subQ14=sQuery(id+"F12.wireOp",EDGE,"E72.1");var subQ16=sQuery(id+"F12.wireOp",EDGE,"E74.1");var subQ18=sQuery(id+"F12.wireOp",EDGE,"E74.8");Q0=qUnion([makeQuery(id+"F12.imprint","IMPRINT",FACE,{"disambiguationData":[TD([[makeQuery(id+"F12.imprint","IMPRINT",EDGE,{"derivedFrom":subQ7}),1.0]])]}),makeQuery(id+"F12.imprint","IMPRINT",FACE,{"disambiguationData":[TD([[makeQuery(id+"F12.imprint","IMPRINT",EDGE,{"derivedFrom":subQ14}),1.0]])]}),makeQuery(id+"F12.imprint","IMPRINT",FACE,{"disambiguationData":[TD([[makeQuery(id+"F12.imprint","IMPRINT",EDGE,{"derivedFrom":subQ16}),1.0]])]}),makeQuery(id+"F12.imprint","IMPRINT",FACE,{"disambiguationData":[TD([[makeQuery(id+"F12.imprint","IMPRINT",EDGE,{"derivedFrom":subQ18}),-1.0]])]})]);}
            var Q1;
            Q1=makeQuery(id+"F5.boolean.opBoolean","SPLIT",FACE,{"disambiguationData":[TD([makeQuery(id+"F5.opExtrude","SWEPT_FACE",FACE,{"disambiguationData":[OSD([sQuery(id+"F4.wireOp",EDGE,"E41")])]})])],"derivedFrom":makeQuery(id+"F3.boolean.opBoolean","COPY",FACE,{"derivedFrom":makeQuery(id+"F3.opExtrude","CAP_FACE",FACE,{"disambiguationData":[OSD([sQuery(id+"F0.wireOp",EDGE,"E25.0"),sQuery(id+"F0.wireOp",EDGE,"E25.1"),sQuery(id+"F0.wireOp",EDGE,"E25.2"),sQuery(id+"F0.wireOp",EDGE,"E25.3"),sQuery(id+"F0.wireOp",EDGE,"E25.4"),sQuery(id+"F0.wireOp",EDGE,"E25.5"),sQuery(id+"F0.wireOp",EDGE,"E25.6"),sQuery(id+"F0.wireOp",EDGE,"E25.7")])],"isStart":false})})});
            extrude(context, id + "F13", {"entities" : qUnion([Q0]), "operationType" : NewBodyOperationType.REMOVE, "endBound" : BoundingType.UP_TO_SURFACE, "endBoundEntityFace" : qUnion([Q1]), "depth" : 25 * mm});
        }
        {
            var Q0;
            Q0=makeQuery(id+"F3.boolean.opBoolean","COPY",EDGE,{"derivedFrom":makeQuery(id+"F3.opExtrude","CAP_EDGE",EDGE,{"disambiguationData":[OSD([sQuery(id+"F0.wireOp",EDGE,"E25.6")])],"isStart":false})});
            var Q1;
            Q1=makeQuery(id+"F8.boolean.opBoolean","INTERSECT",EDGE,{"derivedFrom":[makeQuery(id+"F5.opExtrude","SWEPT_FACE",FACE,{"disambiguationData":[OSD([sQuery(id+"F4.wireOp",EDGE,"E30")])]}),makeQuery(id+"F8.opExtrude","CAP_FACE",FACE,{"disambiguationData":[OSD([sQuery(id+"F7.wireOp",EDGE,"E67")])],"isStart":false})]});
            var Q2;
            Q2=makeQuery(id+"F8.boolean.opBoolean","INTERSECT",EDGE,{"disambiguationData":[OD(1.0)],"derivedFrom":[makeQuery(id+"F5.opExtrude","SWEPT_FACE",FACE,{"disambiguationData":[OSD([sQuery(id+"F4.wireOp",EDGE,"E30")])]}),makeQuery(id+"F8.opExtrude","SWEPT_FACE",FACE,{"disambiguationData":[OSD([sQuery(id+"F7.wireOp",EDGE,"E67")])]})]});
            var Q3;
            {var subQ0=sQuery(id+"F4.wireOp",EDGE,"E30");Q3=makeQuery(id+"F8.boolean.opBoolean","SPLIT",EDGE,{"disambiguationData":[TD([makeQuery(id+"F5.opExtrude","SWEPT_FACE",FACE,{"disambiguationData":[OSD([sQuery(id+"F4.wireOp",EDGE,"E35.filletArc")])]})])],"derivedFrom":makeQuery(id+"F5.opExtrude","CAP_EDGE",EDGE,{"disambiguationData":[OSD([subQ0])],"isStart":false})});}
            var Q4;
            {var subQ0=sQuery(id+"F0.wireOp",EDGE,"E25.7");var subQ1=sQuery(id+"F0.wireOp",EDGE,"E25.1");var subQ2=sQuery(id+"F0.wireOp",EDGE,"E25.6");var subQ3=sQuery(id+"F0.wireOp",EDGE,"E25.5");var subQ4=sQuery(id+"F0.wireOp",EDGE,"E25.4");var subQ5=sQuery(id+"F0.wireOp",EDGE,"E25.0");var subQ6=sQuery(id+"F0.wireOp",EDGE,"E25.2");var subQ7=sQuery(id+"F0.wireOp",EDGE,"E25.3");Q4=makeQuery(id+"F8.boolean.opBoolean","INTERSECT",EDGE,{"derivedFrom":[makeQuery(id+"F5.boolean.opBoolean","SPLIT",FACE,{"disambiguationData":[TD([makeQuery(id+"F2.opExtrude","SWEPT_FACE",FACE,{"disambiguationData":[OSD([subQ5])]})])],"derivedFrom":makeQuery(id+"F3.boolean.opBoolean","COPY",FACE,{"derivedFrom":makeQuery(id+"F3.opExtrude","CAP_FACE",FACE,{"disambiguationData":[OSD([subQ5,subQ1,subQ6,subQ7,subQ4,subQ3,subQ2,subQ0])],"isStart":false})})}),makeQuery(id+"F8.opExtrude","SWEPT_FACE",FACE,{"disambiguationData":[OSD([sQuery(id+"F7.wireOp",EDGE,"E67")])]})]});}
            var Q5;
            Q5=makeQuery(id+"F8.boolean.opBoolean","INTERSECT",EDGE,{"disambiguationData":[OD(0.0)],"derivedFrom":[makeQuery(id+"F5.opExtrude","SWEPT_FACE",FACE,{"disambiguationData":[OSD([sQuery(id+"F4.wireOp",EDGE,"E30")])]}),makeQuery(id+"F8.opExtrude","SWEPT_FACE",FACE,{"disambiguationData":[OSD([sQuery(id+"F7.wireOp",EDGE,"E67")])]})]});
            fillet(context, id + "F14", {"entities" : qUnion([Q0, Q1, Q2, Q3, Q4, Q5]), "radius" : 3 * mm, "tangentPropagation" : true, "allowEdgeOverflow" : false});
        }
        {
            var Q0;
            Q0=makeQuery(id+"F1.opExtrude","CAP_EDGE",EDGE,{"disambiguationData":[OSD([sQuery(id+"F0.wireOp",EDGE,"E1.bottom")])],"isStart":false});
            fillet(context, id + "F15", {"entities" : qUnion([Q0]), "radius" : 2 * mm, "tangentPropagation" : true, "allowEdgeOverflow" : false});
        }
        {
            var Q0;
            {var subQ0=sQuery(id+"F0.wireOp",EDGE,"E22.filletArc");var subQ1=sQuery(id+"F0.wireOp",EDGE,"E7");var subQ2=sQuery(id+"F0.wireOp",EDGE,"E6");var subQ3=sQuery(id+"F0.wireOp",EDGE,"E5");var subQ4=sQuery(id+"F0.wireOp",EDGE,"E4");var subQ5=sQuery(id+"F0.wireOp",EDGE,"E1.bottom");var subQ6=sQuery(id+"F0.wireOp",EDGE,"E21.filletArc");var subQ7=sQuery(id+"F0.wireOp",EDGE,"E1.top");var subQ8=sQuery(id+"F0.wireOp",EDGE,"E1.left");var subQ9=sQuery(id+"F0.wireOp",EDGE,"E1.right");var subQ10=sQuery(id+"F0.wireOp",EDGE,"E23.filletArc");var subQ11=sQuery(id+"F0.wireOp",EDGE,"E24.filletArc");Q0=makeQuery(id+"F2.boolean.opBoolean","SPLIT",FACE,{"disambiguationData":[TD([makeQuery(id+"F1.opExtrude","SWEPT_FACE",FACE,{"disambiguationData":[OSD([subQ5])]})])],"derivedFrom":makeQuery(id+"F1.opExtrude","CAP_FACE",FACE,{"disambiguationData":[OSD([subQ5,subQ7,subQ8,subQ9,subQ4,subQ3,subQ2,subQ1,subQ6,subQ0,subQ10,subQ11])],"isStart":true})});}
            var sketch = newSketch(context, id + "F16", { "sketchPlane" : qUnion([Q0])});
            skLineSegment(sketch, "E79", {"start": v(-25.9, 74.25) * mm, "end": v(-7.9, 92.25) * mm});
            skLineSegment(sketch, "E80", {"start": v(40.1, 74.25) * mm, "end": v(22.1, 92.25) * mm});
            skLineSegment(sketch, "E81", {"start": v(-7.9, 92.25) * mm, "end": v(-7.9, 104.25) * mm});
            skLineSegment(sketch, "E82", {"start": v(22.1, 92.25) * mm, "end": v(22.1, 104.25) * mm});
            skArc(sketch, "E83", {"start": v(22.1, 104.25) * mm, "mid": v(7.1, 119.25) * mm, "end": v(-7.9, 104.25) * mm});
            skCircle(sketch, "E84", {"center": v(7.1, 104.25) * mm, "radius": 6 * mm});
            skLineSegment(sketch, "E85", {"start": v(7.1, 104.25) * mm, "end": v(7.1, 74.25) * mm, "construction": true});
            skPoint(sketch, "E85.endSnap0", {"position": v(0, 74.25) * mm});
            skLineSegment(sketch, "E86", {"start": v(-89.12, 0) * mm, "end": v(122.5, 0) * mm});
            skLineSegment(sketch, "E87.MirrorCS", {"start": v(40.1, -74.25) * mm, "end": v(22.1, -92.25) * mm});
            skLineSegment(sketch, "E88.MirrorCS", {"start": v(22.1, -92.25) * mm, "end": v(22.1, -104.25) * mm});
            skArc(sketch, "E89.MirrorCS", {"start": v(22.1, -104.25) * mm, "mid": v(7.1, -119.25) * mm, "end": v(-7.9, -104.25) * mm});
            skCircle(sketch, "E90.MirrorC", {"center": v(7.1, -104.25) * mm, "radius": 6 * mm});
            skLineSegment(sketch, "E91.MirrorCS", {"start": v(-7.9, -92.25) * mm, "end": v(-7.9, -104.25) * mm});
            skLineSegment(sketch, "E92.MirrorCS", {"start": v(-25.9, -74.25) * mm, "end": v(-7.9, -92.25) * mm});
            skSolve(sketch);
        }
        {
            var Q0;
            {var subQ1=sQuery(id+"F16.wireOp",EDGE,"E79");Q0=makeQuery(id+"F16.imprint","IMPRINT",FACE,{"disambiguationData":[TD([[makeQuery(id+"F16.imprint","IMPRINT",EDGE,{"derivedFrom":subQ1}),-1.0]])]});}
            var Q1;
            {var subQ0=sQuery(id+"F16.wireOp",EDGE,"E87.MirrorCS");Q1=makeQuery(id+"F16.imprint","IMPRINT",FACE,{"disambiguationData":[TD([[makeQuery(id+"F16.imprint","IMPRINT",EDGE,{"derivedFrom":subQ0}),-1.0]])]});}
            var Q2;
            Q2=makeQuery(id+"F2.opExtrude","CAP_FACE",FACE,{"disambiguationData":[OSD([sQuery(id+"F0.wireOp",EDGE,"E12"),sQuery(id+"F0.wireOp",EDGE,"E13"),sQuery(id+"F0.wireOp",EDGE,"E14"),sQuery(id+"F0.wireOp",EDGE,"E15"),sQuery(id+"F0.wireOp",EDGE,"E17.filletArc"),sQuery(id+"F0.wireOp",EDGE,"E18.filletArc"),sQuery(id+"F0.wireOp",EDGE,"E19.filletArc"),sQuery(id+"F0.wireOp",EDGE,"E20.filletArc"),sQuery(id+"F0.wireOp",EDGE,"E25.0"),sQuery(id+"F0.wireOp",EDGE,"E25.1"),sQuery(id+"F0.wireOp",EDGE,"E25.2"),sQuery(id+"F0.wireOp",EDGE,"E25.3"),sQuery(id+"F0.wireOp",EDGE,"E25.4"),sQuery(id+"F0.wireOp",EDGE,"E25.5"),sQuery(id+"F0.wireOp",EDGE,"E25.6"),sQuery(id+"F0.wireOp",EDGE,"E25.7")])],"isStart":false});
            extrude(context, id + "F17", {"entities" : qUnion([Q0, Q1]), "endBound" : BoundingType.UP_TO_SURFACE, "endBoundEntityFace" : qUnion([Q2]), "depth" : 25 * mm});
        }
    });
